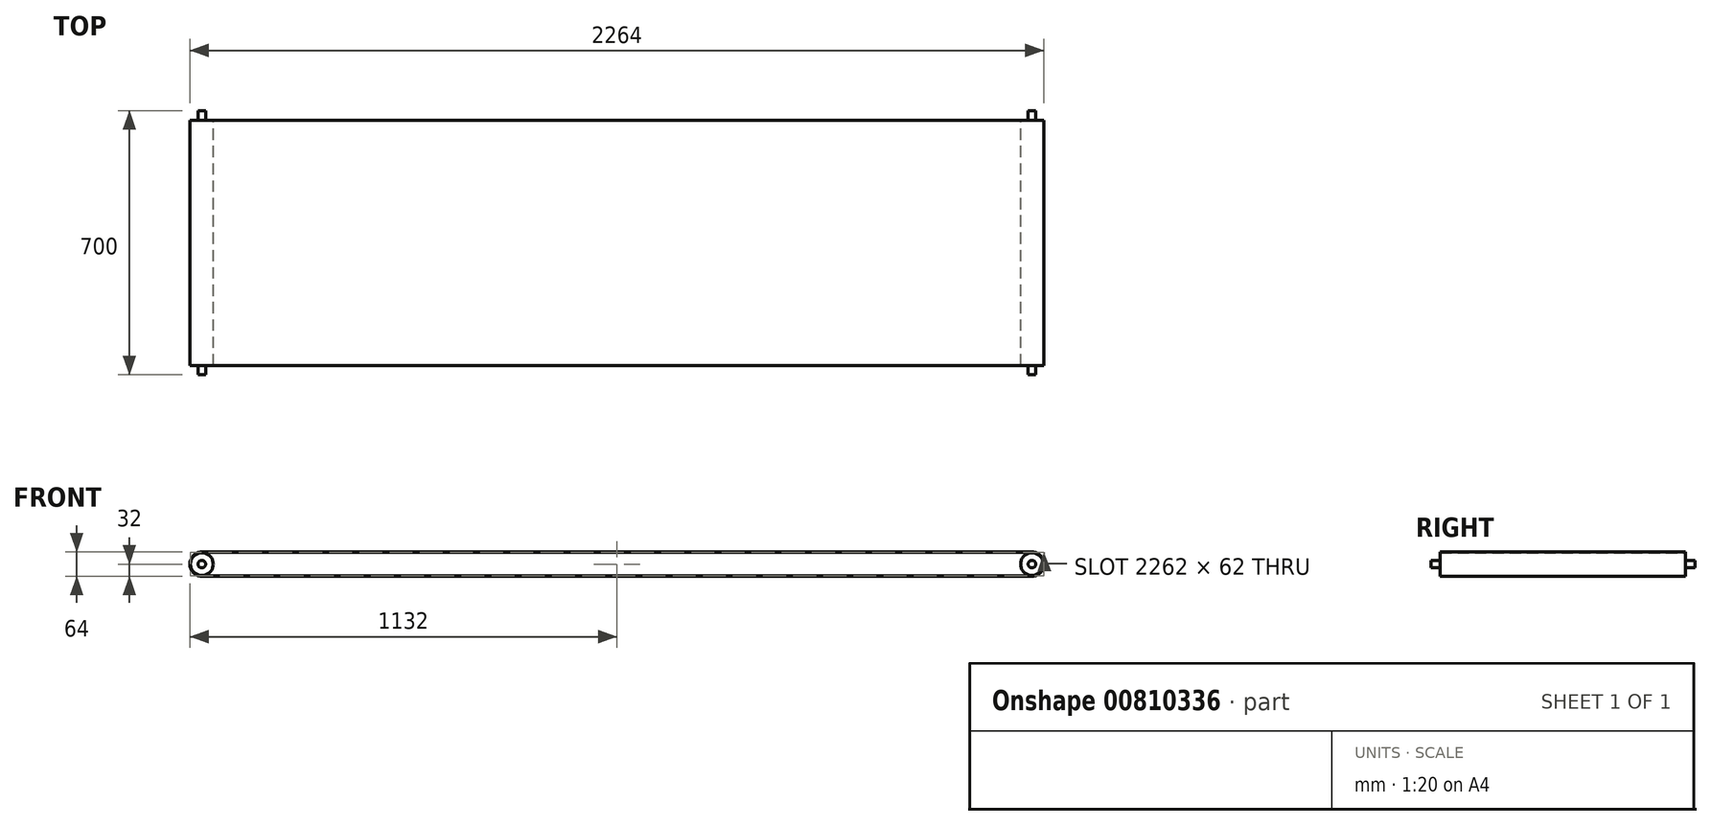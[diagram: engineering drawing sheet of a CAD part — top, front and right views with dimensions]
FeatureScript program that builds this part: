
annotation { "Feature Type Name" : "Feature", "Feature Type Description" : "" }
export const myFeature = defineFeature(function(context is Context, id is Id, definition is map)
    precondition{}
    {
        {
            var Q0;
            Q0=qCreatedBy(makeId("Front.planeOp"),FACE);
            var sketch = newSketch(context, id + "F0", { "sketchPlane" : qUnion([Q0])});
            skCircle(sketch, "E0", {"center": v(0, 0) * mm, "radius": 10 * mm});
            skSolve(sketch);
        }
        {
            var Q0;
            Q0 = qSketchRegion(id + "F0", true);
            extrude(context, id + "F1", {"entities" : qUnion([Q0]), "endBound" : BoundingType.SYMMETRIC, "depth" : 700 * mm, "offsetDistance" : 25.4 * mm});
        }
        {
            var Q0;
            Q0=makeQuery(id+"F1.opExtrude","CAP_FACE",FACE,{"disambiguationData":[OSD([sQuery(id+"F0.wireOp",EDGE,"E0")])],"isStart":false});
            cPlane(context, id + "F2", {"entities" : qUnion([Q0]), "cplaneType" : CPlaneType.OFFSET, "offset" : 350 * mm, "oppositeDirection" : true, "width" : 152.4 * mm, "height" : 152.4 * mm});
        }
        {
            var Q0;
            Q0=qCreatedBy(id+"F2.planeOp",FACE);
            var sketch = newSketch(context, id + "F3", { "sketchPlane" : qUnion([Q0])});
            skCircle(sketch, "E1", {"center": v(0, 0) * mm, "radius": 30 * mm});
            skSolve(sketch);
        }
        {
            var Q0;
            Q0 = qSketchRegion(id + "F3", true);
            extrude(context, id + "F4", {"entities" : qUnion([Q0]), "operationType" : NewBodyOperationType.ADD, "endBound" : BoundingType.SYMMETRIC, "depth" : 650 * mm, "offsetDistance" : 25.4 * mm});
        }
        {
            var Q0;
            Q0=qCreatedBy(makeId("Right.planeOp"),FACE);
            cPlane(context, id + "F5", {"entities" : qUnion([Q0]), "cplaneType" : CPlaneType.OFFSET, "offset" : 1100 * mm, "width" : 152.4 * mm, "height" : 152.4 * mm});
        }
        {
            var Q0;
            Q0=makeQuery(id+"F1.opExtrude","SWEPT_BODY",BODY,{"disambiguationData":[OSD([sQuery(id+"F0.wireOp",EDGE,"E0")])]});
            var Q1;
            Q1=qCreatedBy(id+"F5.planeOp",FACE);
            mirror(context, id + "F6", {"entities" : qUnion([Q0]), "mirrorPlane" : qUnion([Q1])});
        }
        {
            var Q0;
            Q0=makeQuery(id+"F4.opExtrude","CAP_FACE",FACE,{"disambiguationData":[OSD([sQuery(id+"F3.wireOp",EDGE,"E1")])],"isStart":false});
            var sketch = newSketch(context, id + "F7", { "sketchPlane" : qUnion([Q0])});
            skArc(sketch, "E2", {"start": v(0, 32) * mm, "mid": v(-32, 0) * mm, "end": v(0, -32) * mm});
            skLineSegment(sketch, "E3", {"start": v(0, 32) * mm, "end": v(2200, 32) * mm});
            skLineSegment(sketch, "E4", {"start": v(0, -32) * mm, "end": v(2200, -32) * mm});
            skLineSegment(sketch, "E5", {"start": v(2200, -45.5) * mm, "end": v(2200, -333.06) * mm, "construction": true});
            skLineSegment(sketch, "E6", {"start": v(2686.3, 0) * mm, "end": v(2780.44, 0) * mm, "construction": true});
            skArc(sketch, "E7", {"start": v(2200, -32) * mm, "mid": v(2232, 0) * mm, "end": v(2200, 32) * mm});
            skArc(sketch, "E8.0", {"start": v(0, 31) * mm, "mid": v(-31, 0) * mm, "end": v(0, -31) * mm});
            skLineSegment(sketch, "E8.1", {"start": v(0, 31) * mm, "end": v(2200, 31) * mm});
            skArc(sketch, "E8.2", {"start": v(2200, -31) * mm, "mid": v(2231, 0) * mm, "end": v(2200, 31) * mm});
            skLineSegment(sketch, "E8.3", {"start": v(0, -31) * mm, "end": v(2200, -31) * mm});
            skSolve(sketch);
        }
        {
            var Q0;
            Q0 = qSketchRegion(id + "F7", true);
            var Q1;
            Q1=makeQuery(id+"F4.opExtrude","CAP_FACE",FACE,{"disambiguationData":[OSD([sQuery(id+"F3.wireOp",EDGE,"E1")])],"isStart":true});
            extrude(context, id + "F8", {"entities" : qUnion([Q0]), "endBound" : BoundingType.UP_TO_SURFACE, "oppositeDirection" : true, "depth" : 25.4 * mm, "endBoundEntityFace" : qUnion([Q1]), "offsetDistance" : 25.4 * mm});
        }
    });
